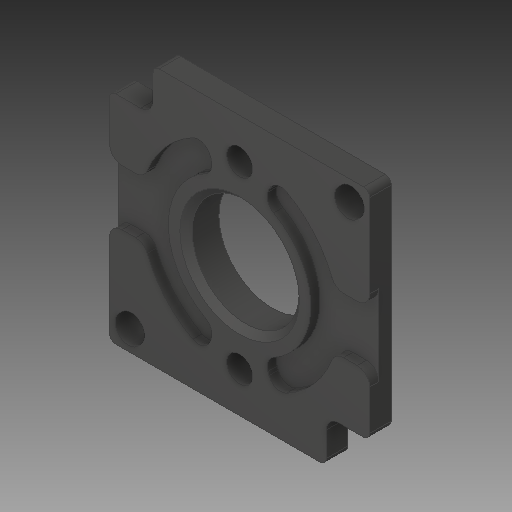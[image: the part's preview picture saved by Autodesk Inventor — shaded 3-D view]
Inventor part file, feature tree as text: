
AUTODESK INVENTOR PART (.ipt)
format: ipt  version: 2018 (Build 220112000, 112)  size: 273,408 bytes
history: native  units: in
note: dims shown in document units (in); Inventor stores cm internally (conversion verified against a paired STEP export)
features: fillet x1
ambient origin geometry x8: Origin, YZ Plane, XZ Plane, XY Plane, X Axis, Y Axis, Z Axis, Center Point
bodies: Solid1 (feature_tree)
feature tree (1):
  fillet  "Fillet4"  [1 undecoded]
note: 1 required parameter value undecoded (feature->parameter linkage not recoverable at this tier; creation-order binding heuristic only, values carry confidence <= 0.55)
